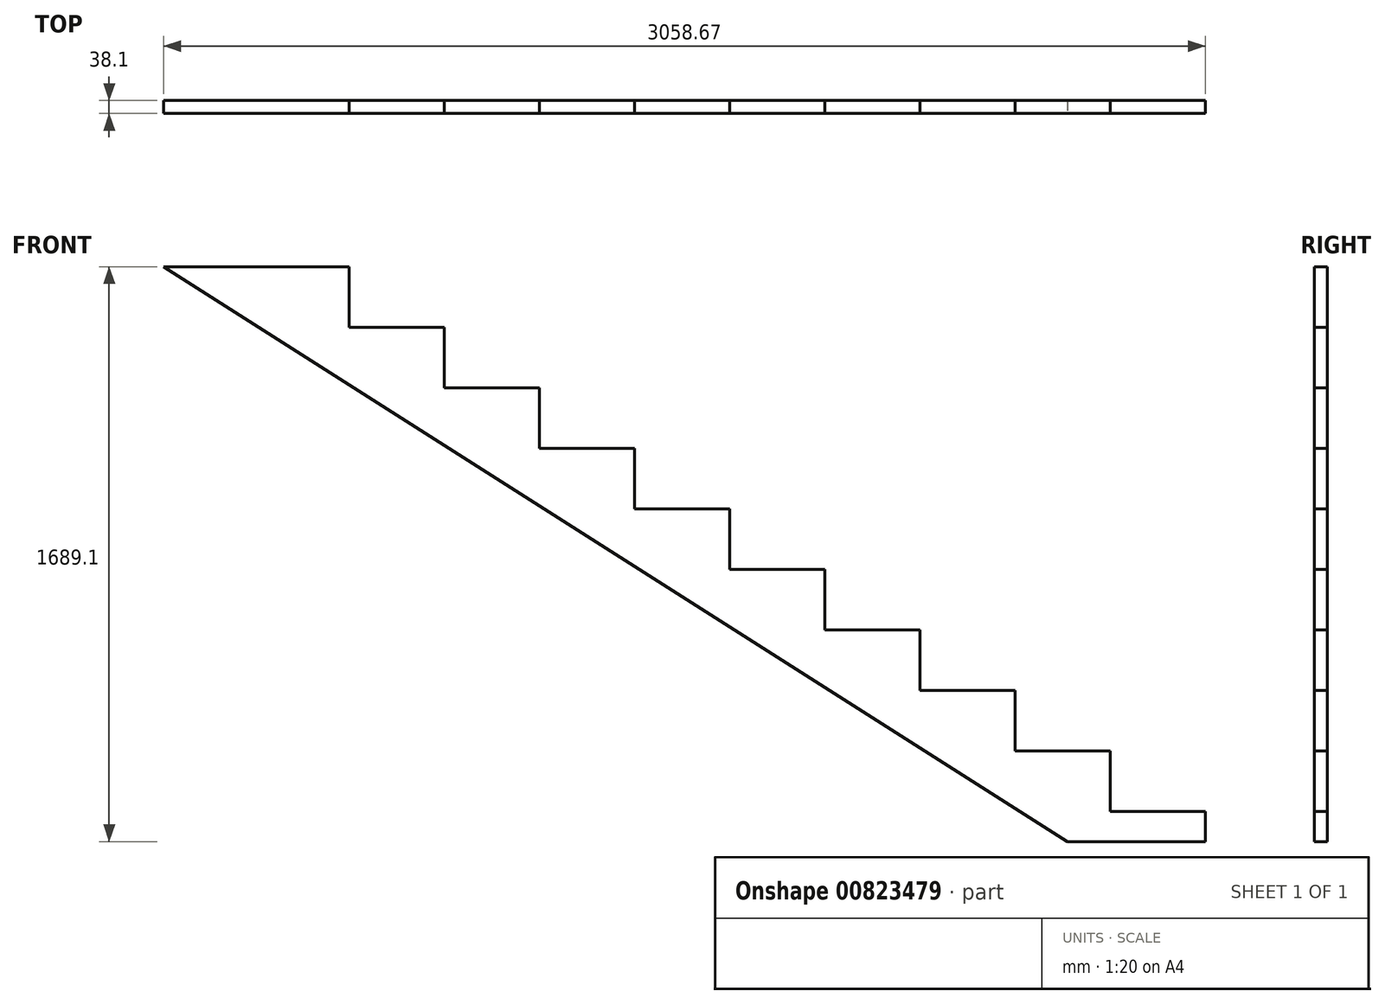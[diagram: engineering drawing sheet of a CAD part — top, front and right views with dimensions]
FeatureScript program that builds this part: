
annotation { "Feature Type Name" : "Feature", "Feature Type Description" : "" }
export const myFeature = defineFeature(function(context is Context, id is Id, definition is map)
    precondition{}
    {
        {
            var Q0;
            Q0=qCreatedBy(makeId("Front.planeOp"),FACE);
            var sketch = newSketch(context, id + "F0", { "sketchPlane" : qUnion([Q0])});
            skLineSegment(sketch, "E0", {"start": v(0, 0) * mm, "end": v(279.4, 0) * mm});
            skLineSegment(sketch, "E1", {"start": v(279.4, 0) * mm, "end": v(279.4, -177.8) * mm});
            skLineSegment(sketch, "E2", {"start": v(279.4, -177.8) * mm, "end": v(558.8, -177.8) * mm});
            skLineSegment(sketch, "E3", {"start": v(0, 0) * mm, "end": v(0, -168.43) * mm});
            skLineSegment(sketch, "E4", {"start": v(0, -168.43) * mm, "end": v(2529.33, -1778) * mm});
            skLineSegment(sketch, "E5", {"start": v(558.8, -177.8) * mm, "end": v(558.8, -355.6) * mm});
            skLineSegment(sketch, "E6", {"start": v(558.8, -355.6) * mm, "end": v(838.2, -355.6) * mm});
            skLineSegment(sketch, "E7", {"start": v(838.2, -355.6) * mm, "end": v(838.2, -533.4) * mm});
            skLineSegment(sketch, "E8", {"start": v(838.2, -533.4) * mm, "end": v(1117.6, -533.4) * mm});
            skLineSegment(sketch, "E9", {"start": v(1117.6, -533.4) * mm, "end": v(1117.6, -711.2) * mm});
            skLineSegment(sketch, "E10", {"start": v(1117.6, -711.2) * mm, "end": v(1397, -711.2) * mm});
            skLineSegment(sketch, "E11", {"start": v(1397, -711.2) * mm, "end": v(1397, -889) * mm});
            skLineSegment(sketch, "E12", {"start": v(1397, -889) * mm, "end": v(1676.4, -889) * mm});
            skLineSegment(sketch, "E13", {"start": v(1676.4, -889) * mm, "end": v(1676.4, -1066.8) * mm});
            skLineSegment(sketch, "E14", {"start": v(1676.4, -1066.8) * mm, "end": v(1955.8, -1066.8) * mm});
            skLineSegment(sketch, "E15", {"start": v(1955.8, -1066.8) * mm, "end": v(1955.8, -1244.6) * mm});
            skLineSegment(sketch, "E16", {"start": v(1955.8, -1244.6) * mm, "end": v(2235.2, -1244.6) * mm});
            skLineSegment(sketch, "E17", {"start": v(2235.2, -1244.6) * mm, "end": v(2235.2, -1422.4) * mm});
            skLineSegment(sketch, "E18", {"start": v(2235.2, -1422.4) * mm, "end": v(2514.6, -1422.4) * mm});
            skLineSegment(sketch, "E19", {"start": v(2514.6, -1422.4) * mm, "end": v(2514.6, -1600.2) * mm});
            skLineSegment(sketch, "E20", {"start": v(2514.6, -1600.2) * mm, "end": v(2794, -1600.2) * mm});
            skLineSegment(sketch, "E21", {"start": v(2794, -1600.2) * mm, "end": v(2794, -1778) * mm});
            skLineSegment(sketch, "E22", {"start": v(2794, -1778) * mm, "end": v(2529.33, -1778) * mm});
            skLineSegment(sketch, "E23", {"start": v(279.4, 0) * mm, "end": v(2794, -1600.2) * mm, "construction": true});
            skSolve(sketch);
        }
        {
            var Q0;
            Q0=qSketchRegion(id+"F0",true);
            extrude(context, id + "F1", {"entities" : qUnion([Q0]), "depth" : 38.1 * mm, "offsetDistance" : 25.4 * mm});
        }
        {
            var Q0;
            Q0=makeQuery(id+"F1.opExtrude","CAP_FACE",FACE,{"disambiguationData":[OSD([sQuery(id+"F0.wireOp",EDGE,"E0"),sQuery(id+"F0.wireOp",EDGE,"E1"),sQuery(id+"F0.wireOp",EDGE,"E2"),sQuery(id+"F0.wireOp",EDGE,"E3"),sQuery(id+"F0.wireOp",EDGE,"E4"),sQuery(id+"F0.wireOp",EDGE,"E5"),sQuery(id+"F0.wireOp",EDGE,"E6"),sQuery(id+"F0.wireOp",EDGE,"E7"),sQuery(id+"F0.wireOp",EDGE,"E8"),sQuery(id+"F0.wireOp",EDGE,"E9"),sQuery(id+"F0.wireOp",EDGE,"E10"),sQuery(id+"F0.wireOp",EDGE,"E11"),sQuery(id+"F0.wireOp",EDGE,"E12"),sQuery(id+"F0.wireOp",EDGE,"E13"),sQuery(id+"F0.wireOp",EDGE,"E14"),sQuery(id+"F0.wireOp",EDGE,"E15"),sQuery(id+"F0.wireOp",EDGE,"E16"),sQuery(id+"F0.wireOp",EDGE,"E17"),sQuery(id+"F0.wireOp",EDGE,"E18"),sQuery(id+"F0.wireOp",EDGE,"E19"),sQuery(id+"F0.wireOp",EDGE,"E20"),sQuery(id+"F0.wireOp",EDGE,"E21"),sQuery(id+"F0.wireOp",EDGE,"E22")])],"isStart":false});
            var sketch = newSketch(context, id + "F2", { "sketchPlane" : qUnion([Q0])});
            skLineSegment(sketch, "E24", {"start": v(0, 0) * mm, "end": v(-264.67, 0) * mm});
            skLineSegment(sketch, "E25", {"start": v(-264.67, 0) * mm, "end": v(0, -168.43) * mm});
            skLineSegment(sketch, "E26", {"start": v(0, -168.43) * mm, "end": v(0, 0) * mm});
            skSolve(sketch);
        }
        {
            var Q0;
            Q0 = qSketchRegion(id + "F2", true);
            extrude(context, id + "F3", {"entities" : qUnion([Q0]), "operationType" : NewBodyOperationType.ADD, "oppositeDirection" : true, "depth" : 38.1 * mm, "offsetDistance" : 25.4 * mm});
        }
        {
            var Q0;
            Q0=makeQuery(id+"F3.boolean.opBoolean","MERGE",FACE,{"derivedFrom":[makeQuery(id+"F1.opExtrude","CAP_FACE",FACE,{"disambiguationData":[OSD([sQuery(id+"F0.wireOp",EDGE,"E0"),sQuery(id+"F0.wireOp",EDGE,"E1"),sQuery(id+"F0.wireOp",EDGE,"E2"),sQuery(id+"F0.wireOp",EDGE,"E3"),sQuery(id+"F0.wireOp",EDGE,"E4"),sQuery(id+"F0.wireOp",EDGE,"E5"),sQuery(id+"F0.wireOp",EDGE,"E6"),sQuery(id+"F0.wireOp",EDGE,"E7"),sQuery(id+"F0.wireOp",EDGE,"E8"),sQuery(id+"F0.wireOp",EDGE,"E9"),sQuery(id+"F0.wireOp",EDGE,"E10"),sQuery(id+"F0.wireOp",EDGE,"E11"),sQuery(id+"F0.wireOp",EDGE,"E12"),sQuery(id+"F0.wireOp",EDGE,"E13"),sQuery(id+"F0.wireOp",EDGE,"E14"),sQuery(id+"F0.wireOp",EDGE,"E15"),sQuery(id+"F0.wireOp",EDGE,"E16"),sQuery(id+"F0.wireOp",EDGE,"E17"),sQuery(id+"F0.wireOp",EDGE,"E18"),sQuery(id+"F0.wireOp",EDGE,"E19"),sQuery(id+"F0.wireOp",EDGE,"E20"),sQuery(id+"F0.wireOp",EDGE,"E21"),sQuery(id+"F0.wireOp",EDGE,"E22")])],"isStart":false}),makeQuery(id+"F3.opExtrude","CAP_FACE",FACE,{"disambiguationData":[OSD([sQuery(id+"F2.wireOp",EDGE,"E24"),sQuery(id+"F2.wireOp",EDGE,"E25"),sQuery(id+"F2.wireOp",EDGE,"E26")])],"isStart":true})]});
            var sketch = newSketch(context, id + "F4", { "sketchPlane" : qUnion([Q0])});
            skLineSegment(sketch, "E27", {"start": v(2794, -1689.1) * mm, "end": v(2389.63, -1689.1) * mm});
            skLineSegment(sketch, "E28", {"start": v(2389.63, -1689.1) * mm, "end": v(2529.33, -1778) * mm});
            skLineSegment(sketch, "E29", {"start": v(2529.33, -1778) * mm, "end": v(2794, -1778) * mm});
            skLineSegment(sketch, "E30", {"start": v(2794, -1778) * mm, "end": v(2794, -1689.1) * mm});
            skSolve(sketch);
        }
        {
            var Q0;
            Q0 = qSketchRegion(id + "F4", true);
            extrude(context, id + "F5", {"entities" : qUnion([Q0]), "operationType" : NewBodyOperationType.REMOVE, "endBound" : BoundingType.THROUGH_ALL, "oppositeDirection" : true, "depth" : 25.4 * mm, "offsetDistance" : 25.4 * mm});
        }
    });
